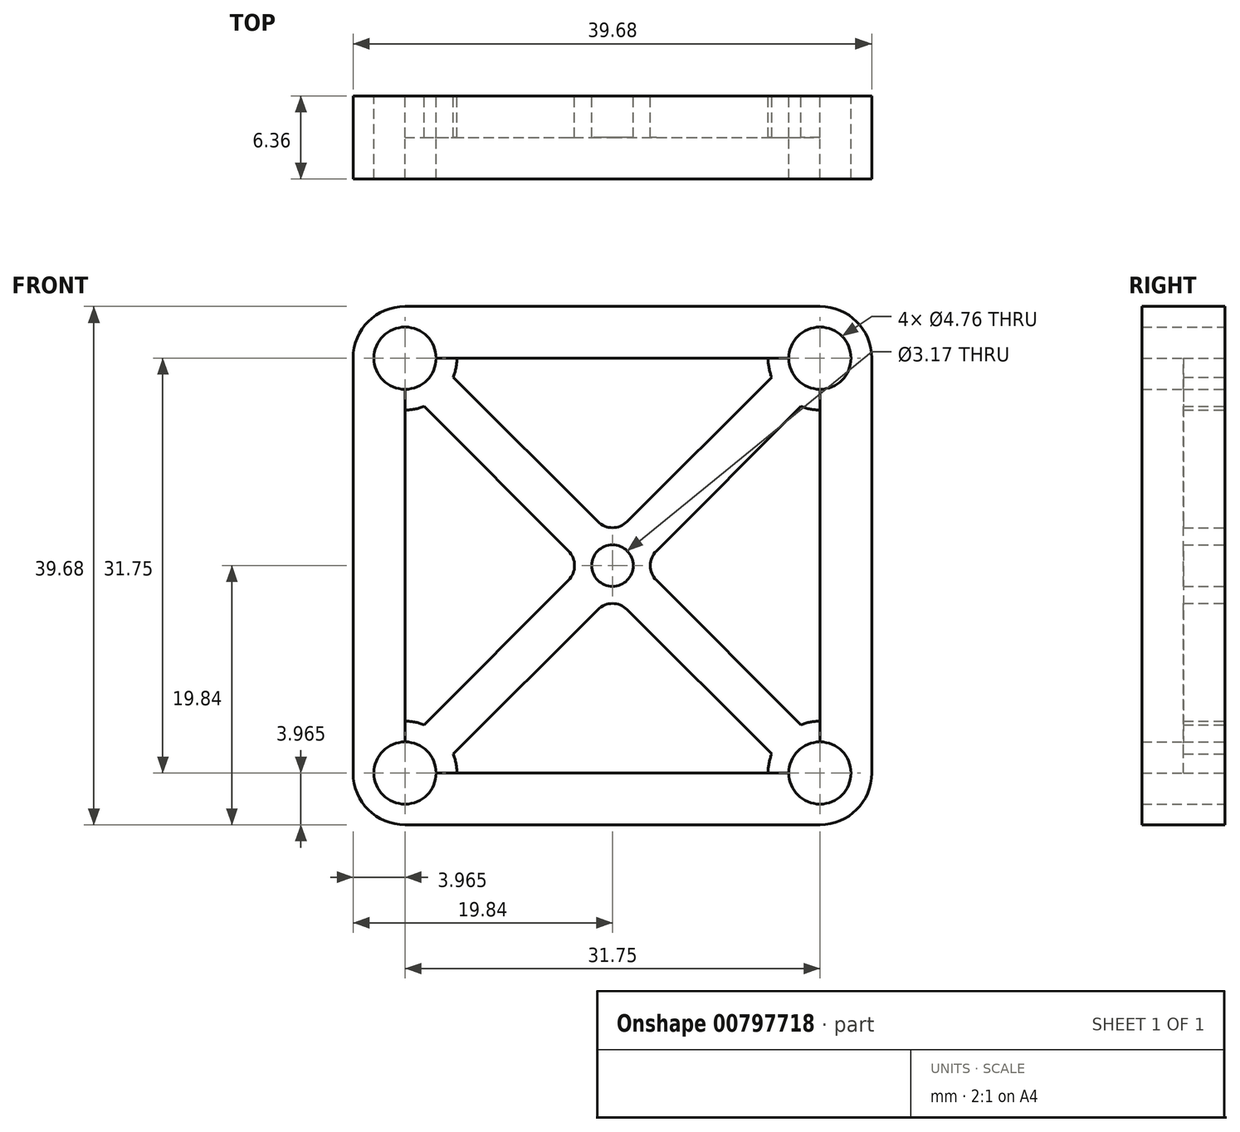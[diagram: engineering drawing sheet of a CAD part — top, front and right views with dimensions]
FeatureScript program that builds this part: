
annotation { "Feature Type Name" : "Feature", "Feature Type Description" : "" }
export const myFeature = defineFeature(function(context is Context, id is Id, definition is map)
    precondition{}
    {
        {
            var Q0;
            Q0=qCreatedBy(makeId("Front.planeOp"),FACE);
            var sketch = newSketch(context, id + "F0", { "sketchPlane" : qUnion([Q0])});
            skLineSegment(sketch, "E0.bottom", {"start": v(-15.87, 15.88) * mm, "end": v(15.88, 15.88) * mm, "construction": true});
            skLineSegment(sketch, "E0.top", {"start": v(-15.88, -15.88) * mm, "end": v(15.87, -15.88) * mm, "construction": true});
            skLineSegment(sketch, "E0.left", {"start": v(-15.87, 15.88) * mm, "end": v(-15.88, -15.88) * mm, "construction": true});
            skLineSegment(sketch, "E0.right", {"start": v(15.88, 15.88) * mm, "end": v(15.87, -15.88) * mm, "construction": true});
            skPoint(sketch, "E0.middle", {"position": v(0, 0) * mm});
            skCircle(sketch, "E1", {"center": v(-15.87, 15.88) * mm, "radius": 2.38 * mm});
            skCircle(sketch, "E2", {"center": v(-15.88, -15.88) * mm, "radius": 2.38 * mm});
            skCircle(sketch, "E3", {"center": v(15.87, -15.88) * mm, "radius": 2.38 * mm});
            skCircle(sketch, "E4", {"center": v(15.88, 15.88) * mm, "radius": 2.38 * mm});
            skArc(sketch, "E5", {"start": v(-15.88, 19.84) * mm, "mid": v(-18.68, 18.68) * mm, "end": v(-19.84, 15.88) * mm});
            skArc(sketch, "E6", {"start": v(-19.84, -15.88) * mm, "mid": v(-18.68, -18.68) * mm, "end": v(-15.88, -19.84) * mm});
            skArc(sketch, "E7", {"start": v(15.88, -19.84) * mm, "mid": v(18.68, -18.68) * mm, "end": v(19.84, -15.87) * mm});
            skArc(sketch, "E8", {"start": v(19.84, 15.88) * mm, "mid": v(18.68, 18.68) * mm, "end": v(15.88, 19.84) * mm});
            skLineSegment(sketch, "E9", {"start": v(-19.84, 15.88) * mm, "end": v(-19.84, -15.88) * mm});
            skLineSegment(sketch, "E10", {"start": v(-15.88, -19.84) * mm, "end": v(15.88, -19.84) * mm});
            skLineSegment(sketch, "E11", {"start": v(19.84, -15.87) * mm, "end": v(19.84, 15.88) * mm});
            skLineSegment(sketch, "E12", {"start": v(-15.88, 19.84) * mm, "end": v(15.88, 19.84) * mm});
            skLineSegment(sketch, "E13", {"start": v(-15.88, -11.9) * mm, "end": v(-15.88, 11.9) * mm});
            skLineSegment(sketch, "E14", {"start": v(-11.9, 15.88) * mm, "end": v(11.9, 15.88) * mm});
            skLineSegment(sketch, "E15", {"start": v(15.88, 11.9) * mm, "end": v(15.88, -11.9) * mm});
            skLineSegment(sketch, "E16", {"start": v(11.9, -15.88) * mm, "end": v(-11.9, -15.88) * mm});
            skArc(sketch, "E17.trimOffspring", {"start": v(-15.88, 11.9) * mm, "mid": v(-15.14, 11.98) * mm, "end": v(-14.43, 12.18) * mm});
            skArc(sketch, "E18.trimOffspring", {"start": v(-11.9, -15.88) * mm, "mid": v(-11.98, -15.14) * mm, "end": v(-12.18, -14.43) * mm});
            skArc(sketch, "E19.trimOffspring", {"start": v(15.88, -11.9) * mm, "mid": v(15.14, -11.98) * mm, "end": v(14.43, -12.18) * mm});
            skArc(sketch, "E20.trimOffspring", {"start": v(11.9, 15.88) * mm, "mid": v(11.98, 15.14) * mm, "end": v(12.18, 14.43) * mm});
            skLineSegment(sketch, "E21", {"start": v(-14.43, 12.18) * mm, "end": v(-3.37, 1.12) * mm});
            skLineSegment(sketch, "E22", {"start": v(12.18, 14.43) * mm, "end": v(1.12, 3.37) * mm});
            skLineSegment(sketch, "E23", {"start": v(-12.18, -14.43) * mm, "end": v(-1.12, -3.37) * mm});
            skLineSegment(sketch, "E24", {"start": v(-15.87, 15.88) * mm, "end": v(15.87, -15.88) * mm, "construction": true});
            skLineSegment(sketch, "E25", {"start": v(15.88, 15.88) * mm, "end": v(-15.88, -15.88) * mm, "construction": true});
            skLineSegment(sketch, "E26", {"start": v(-12.18, 14.43) * mm, "end": v(-1.12, 3.37) * mm});
            skLineSegment(sketch, "E27.trimOffspring", {"start": v(-3.37, -1.12) * mm, "end": v(-14.43, -12.18) * mm});
            skLineSegment(sketch, "E28.trimOffspring", {"start": v(3.37, 1.12) * mm, "end": v(14.43, 12.18) * mm});
            skLineSegment(sketch, "E29.trimOffspring", {"start": v(3.37, -1.12) * mm, "end": v(14.43, -12.18) * mm});
            skLineSegment(sketch, "E30.trimOffspring", {"start": v(1.12, -3.37) * mm, "end": v(12.18, -14.43) * mm});
            skPoint(sketch, "E31.visualSharp", {"position": v(-2.25, 0) * mm});
            skArc(sketch, "E31.filletArc", {"start": v(-3.37, -1.12) * mm, "mid": v(-2.9, 0) * mm, "end": v(-3.37, 1.12) * mm});
            skPoint(sketch, "E32.visualSharp", {"position": v(0, -2.25) * mm});
            skArc(sketch, "E32.filletArc", {"start": v(1.12, -3.37) * mm, "mid": v(0, -2.9) * mm, "end": v(-1.12, -3.37) * mm});
            skPoint(sketch, "E33.visualSharp", {"position": v(2.25, 0) * mm});
            skArc(sketch, "E33.filletArc", {"start": v(3.37, 1.12) * mm, "mid": v(2.9, 0) * mm, "end": v(3.37, -1.12) * mm});
            skPoint(sketch, "E34.visualSharp", {"position": v(0, 2.25) * mm});
            skArc(sketch, "E34.filletArc", {"start": v(-1.12, 3.37) * mm, "mid": v(0, 2.9) * mm, "end": v(1.12, 3.37) * mm});
            skCircle(sketch, "E35", {"center": v(0, 0) * mm, "radius": 1.59 * mm});
            skArc(sketch, "E36.trimOffspring", {"start": v(-12.18, 14.43) * mm, "mid": v(-11.98, 15.14) * mm, "end": v(-11.9, 15.88) * mm});
            skArc(sketch, "E37.trimOffspring", {"start": v(-14.43, -12.18) * mm, "mid": v(-15.14, -11.98) * mm, "end": v(-15.88, -11.9) * mm});
            skArc(sketch, "E38.trimOffspring", {"start": v(12.18, -14.43) * mm, "mid": v(11.98, -15.14) * mm, "end": v(11.9, -15.87) * mm});
            skArc(sketch, "E39.trimOffspring", {"start": v(14.43, 12.18) * mm, "mid": v(15.14, 11.98) * mm, "end": v(15.88, 11.9) * mm});
            skSolve(sketch);
        }
        {
            var Q0;
            Q0=makeQuery(id+"F0.imprint","IMPRINT",FACE,{"disambiguationData":[TD([[makeQuery(id+"F0.imprint","IMPRINT",EDGE,{"derivedFrom":sQuery(id+"F0.wireOp",EDGE,"E1")}),-1.0]])]});
            extrude(context, id + "F1", {"entities" : qUnion([Q0]), "endBound" : BoundingType.SYMMETRIC, "depth" : 6.35 * mm, "offsetDistance" : 25.4 * mm});
        }
        {
            var Q0;
            Q0=makeQuery(id+"F1.opExtrude","CAP_FACE",FACE,{"disambiguationData":[OSD([sQuery(id+"F0.wireOp",EDGE,"E1"),sQuery(id+"F0.wireOp",EDGE,"E2"),sQuery(id+"F0.wireOp",EDGE,"E3"),sQuery(id+"F0.wireOp",EDGE,"E4"),sQuery(id+"F0.wireOp",EDGE,"E5"),sQuery(id+"F0.wireOp",EDGE,"E6"),sQuery(id+"F0.wireOp",EDGE,"E7"),sQuery(id+"F0.wireOp",EDGE,"E8"),sQuery(id+"F0.wireOp",EDGE,"E9"),sQuery(id+"F0.wireOp",EDGE,"E10"),sQuery(id+"F0.wireOp",EDGE,"E11"),sQuery(id+"F0.wireOp",EDGE,"E12"),sQuery(id+"F0.wireOp",EDGE,"E13"),sQuery(id+"F0.wireOp",EDGE,"E14"),sQuery(id+"F0.wireOp",EDGE,"E15"),sQuery(id+"F0.wireOp",EDGE,"E16"),sQuery(id+"F0.wireOp",EDGE,"E17.trimOffspring"),sQuery(id+"F0.wireOp",EDGE,"E18.trimOffspring"),sQuery(id+"F0.wireOp",EDGE,"E19.trimOffspring"),sQuery(id+"F0.wireOp",EDGE,"E20.trimOffspring"),sQuery(id+"F0.wireOp",EDGE,"E21"),sQuery(id+"F0.wireOp",EDGE,"E22"),sQuery(id+"F0.wireOp",EDGE,"E23"),sQuery(id+"F0.wireOp",EDGE,"E26"),sQuery(id+"F0.wireOp",EDGE,"E27.trimOffspring"),sQuery(id+"F0.wireOp",EDGE,"E28.trimOffspring"),sQuery(id+"F0.wireOp",EDGE,"E29.trimOffspring"),sQuery(id+"F0.wireOp",EDGE,"E30.trimOffspring"),sQuery(id+"F0.wireOp",EDGE,"E31.filletArc"),sQuery(id+"F0.wireOp",EDGE,"E32.filletArc"),sQuery(id+"F0.wireOp",EDGE,"E33.filletArc"),sQuery(id+"F0.wireOp",EDGE,"E34.filletArc"),sQuery(id+"F0.wireOp",EDGE,"E35"),sQuery(id+"F0.wireOp",EDGE,"E36.trimOffspring"),sQuery(id+"F0.wireOp",EDGE,"E37.trimOffspring"),sQuery(id+"F0.wireOp",EDGE,"E38.trimOffspring"),sQuery(id+"F0.wireOp",EDGE,"E39.trimOffspring")])],"isStart":false});
            var sketch = newSketch(context, id + "F2", { "sketchPlane" : qUnion([Q0])});
            skLineSegment(sketch, "E40.0", {"start": v(-15.88, -11.9) * mm, "end": v(-15.88, 11.9) * mm, "construction": true});
            skLineSegment(sketch, "E41.0", {"start": v(-11.9, 15.88) * mm, "end": v(11.9, 15.88) * mm, "construction": true});
            skLineSegment(sketch, "E42.bottom", {"start": v(-15.87, 15.88) * mm, "end": v(15.87, 15.88) * mm});
            skLineSegment(sketch, "E42.top", {"start": v(-15.87, -15.88) * mm, "end": v(15.87, -15.88) * mm});
            skLineSegment(sketch, "E42.left", {"start": v(-15.87, 15.88) * mm, "end": v(-15.87, -15.88) * mm});
            skLineSegment(sketch, "E42.right", {"start": v(15.87, 15.88) * mm, "end": v(15.87, -15.88) * mm});
            skPoint(sketch, "E42.middle", {"position": v(0, 0) * mm});
            skCircle(sketch, "E43.0", {"center": v(-15.87, 15.88) * mm, "radius": 2.38 * mm});
            skCircle(sketch, "E44.0", {"center": v(15.88, 15.88) * mm, "radius": 2.38 * mm});
            skCircle(sketch, "E45.0", {"center": v(15.87, -15.88) * mm, "radius": 2.38 * mm});
            skCircle(sketch, "E46.0", {"center": v(-15.88, -15.88) * mm, "radius": 2.38 * mm});
            skSolve(sketch);
        }
        {
            var Q0;
            {var subQ19=makeQuery(id+"F1.opExtrude","CAP_EDGE",EDGE,{"disambiguationData":[OSD([sQuery(id+"F0.wireOp",EDGE,"E17.trimOffspring")])],"isStart":false});Q0=makeQuery(id+"F2.imprint","IMPRINT",FACE,{"disambiguationData":[TD([[makeQuery(id+"F2.imprint","IMPRINT",EDGE,{"derivedFrom":subQ19}),1.0]])]});}
            var Q1;
            {var subQ0=sQuery(id+"F2.wireOp",EDGE,"E42.left");var subQ1=sQuery(id+"F2.wireOp",EDGE,"E42.bottom");var subQ2=makeQuery(id+"F2.imprint","INTERSECT",VERTEX,{"derivedFrom":[subQ1,subQ0]});Q1=makeQuery(id+"F2.imprint","IMPRINT",FACE,{"disambiguationData":[TD([[makeQuery(id+"F2.imprint","IMPRINT",EDGE,{"disambiguationData":[TD([[subQ2,-1.0]])],"derivedFrom":subQ1}),-1.0]])]});}
            var Q2;
            {var subQ0=makeQuery(id+"F1.opExtrude","CAP_EDGE",EDGE,{"disambiguationData":[OSD([sQuery(id+"F0.wireOp",EDGE,"E17.trimOffspring")])],"isStart":false});Q2=makeQuery(id+"F2.imprint","IMPRINT",FACE,{"disambiguationData":[TD([[makeQuery(id+"F2.imprint","IMPRINT",EDGE,{"derivedFrom":subQ0}),-1.0]])]});}
            var Q3;
            {var subQ0=makeQuery(id+"F1.opExtrude","CAP_EDGE",EDGE,{"disambiguationData":[OSD([sQuery(id+"F0.wireOp",EDGE,"E20.trimOffspring")])],"isStart":false});Q3=makeQuery(id+"F2.imprint","IMPRINT",FACE,{"disambiguationData":[TD([[makeQuery(id+"F2.imprint","IMPRINT",EDGE,{"derivedFrom":subQ0}),-1.0]])]});}
            var Q4;
            {var subQ0=sQuery(id+"F2.wireOp",EDGE,"E42.right");var subQ1=sQuery(id+"F2.wireOp",EDGE,"E42.bottom");var subQ2=makeQuery(id+"F2.imprint","INTERSECT",VERTEX,{"derivedFrom":[subQ1,subQ0]});Q4=makeQuery(id+"F2.imprint","IMPRINT",FACE,{"disambiguationData":[TD([[makeQuery(id+"F2.imprint","IMPRINT",EDGE,{"disambiguationData":[TD([[subQ2,1.0]])],"derivedFrom":subQ1}),-1.0]])]});}
            var Q5;
            {var subQ1=makeQuery(id+"F1.opExtrude","CAP_EDGE",EDGE,{"disambiguationData":[OSD([sQuery(id+"F0.wireOp",EDGE,"E19.trimOffspring")])],"isStart":false});Q5=makeQuery(id+"F2.imprint","IMPRINT",FACE,{"disambiguationData":[TD([[makeQuery(id+"F2.imprint","IMPRINT",EDGE,{"derivedFrom":subQ1}),-1.0]])]});}
            var Q6;
            {var subQ0=makeQuery(id+"F1.opExtrude","CAP_EDGE",EDGE,{"disambiguationData":[OSD([sQuery(id+"F0.wireOp",EDGE,"E18.trimOffspring")])],"isStart":false});Q6=makeQuery(id+"F2.imprint","IMPRINT",FACE,{"disambiguationData":[TD([[makeQuery(id+"F2.imprint","IMPRINT",EDGE,{"derivedFrom":subQ0}),-1.0]])]});}
            var Q7;
            {var subQ0=sQuery(id+"F2.wireOp",EDGE,"E42.right");var subQ1=sQuery(id+"F2.wireOp",EDGE,"E42.top");var subQ2=makeQuery(id+"F2.imprint","INTERSECT",VERTEX,{"derivedFrom":[subQ1,subQ0]});var subQ3=sQuery(id+"F2.wireOp",EDGE,"E45.0");var subQ4=makeQuery(id+"F2.imprint","INTERSECT",VERTEX,{"derivedFrom":[subQ1,subQ3]});Q7=makeQuery(id+"F2.imprint","IMPRINT",FACE,{"disambiguationData":[TD([[makeQuery(id+"F2.imprint","IMPRINT",EDGE,{"disambiguationData":[TD([[subQ2,1.0],[subQ4,-1.0]])],"derivedFrom":subQ1}),1.0]])]});}
            var Q8;
            {var subQ0=sQuery(id+"F2.wireOp",EDGE,"E42.left");var subQ1=sQuery(id+"F2.wireOp",EDGE,"E42.top");var subQ2=makeQuery(id+"F2.imprint","INTERSECT",VERTEX,{"derivedFrom":[subQ1,subQ0]});var subQ3=sQuery(id+"F2.wireOp",EDGE,"E46.0");var subQ4=makeQuery(id+"F2.imprint","INTERSECT",VERTEX,{"derivedFrom":[subQ1,subQ3]});Q8=makeQuery(id+"F2.imprint","IMPRINT",FACE,{"disambiguationData":[TD([[makeQuery(id+"F2.imprint","IMPRINT",EDGE,{"disambiguationData":[TD([[subQ2,-1.0],[subQ4,1.0]])],"derivedFrom":subQ1}),1.0]])]});}
            var Q9;
            Q9=makeQuery(id+"F2.imprint","IMPRINT",FACE,{"disambiguationData":[TD([[makeQuery(id+"F2.imprint","IMPRINT",EDGE,{"derivedFrom":makeQuery(id+"F1.opExtrude","CAP_EDGE",EDGE,{"disambiguationData":[OSD([sQuery(id+"F0.wireOp",EDGE,"E35")])],"isStart":false})}),1.0]])]});
            extrude(context, id + "F3", {"entities" : qUnion([Q0, Q1, Q2, Q3, Q4, Q5, Q6, Q7, Q8, Q9]), "operationType" : NewBodyOperationType.REMOVE, "oppositeDirection" : true, "depth" : 3.17 * mm, "offsetDistance" : 25.4 * mm});
        }
    });
